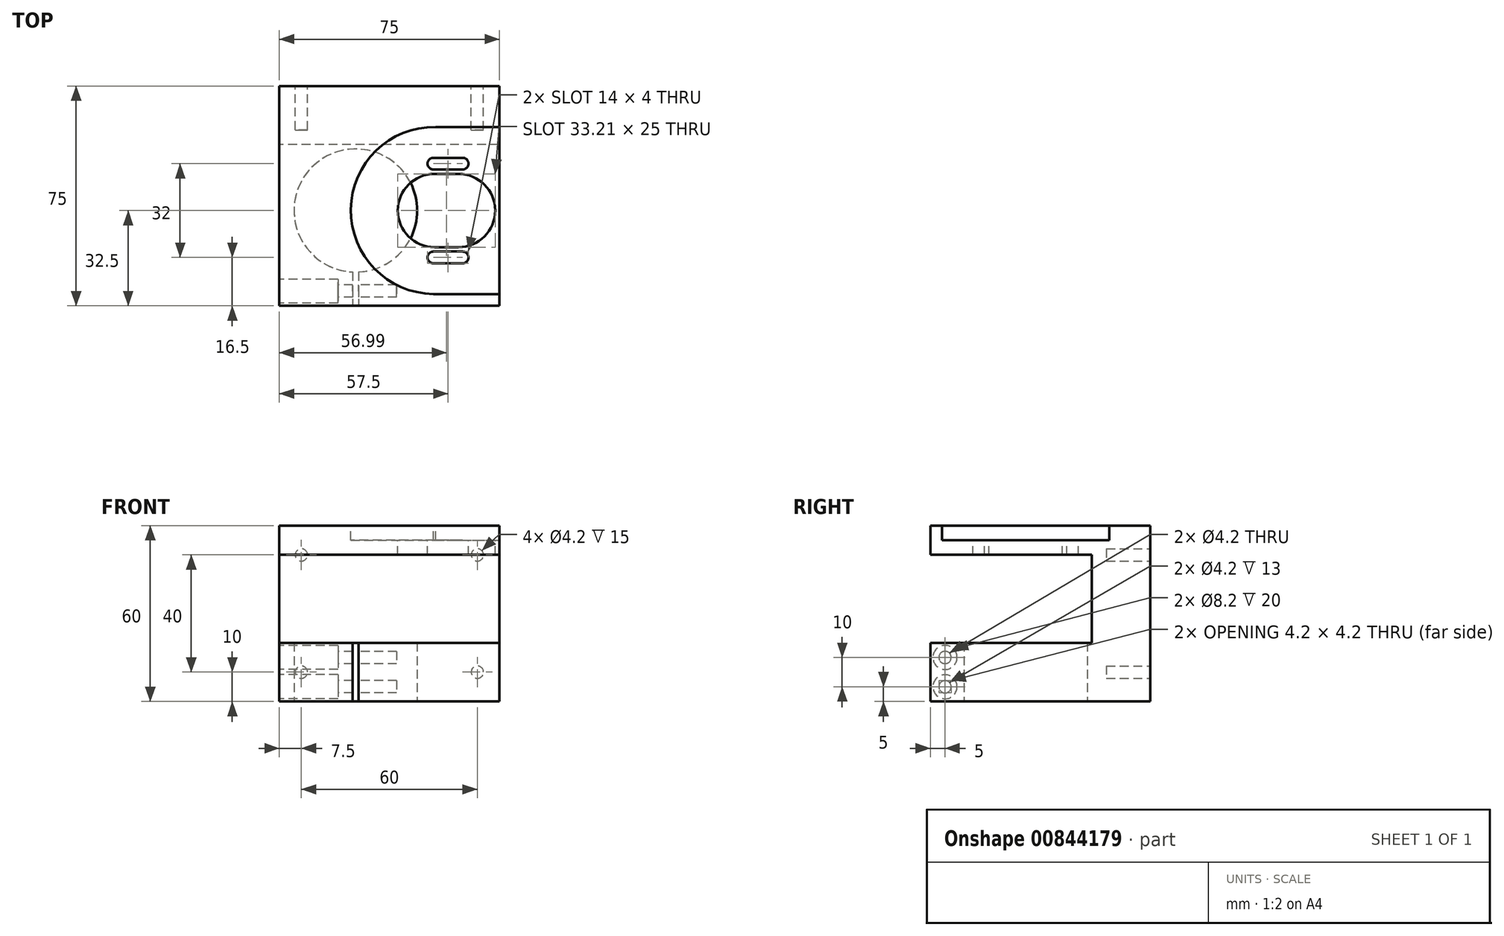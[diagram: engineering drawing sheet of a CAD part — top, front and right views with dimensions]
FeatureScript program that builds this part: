
annotation { "Feature Type Name" : "Feature", "Feature Type Description" : "" }
export const myFeature = defineFeature(function(context is Context, id is Id, definition is map)
    precondition{}
    {
        {
            var Q0;
            Q0=qCreatedBy(makeId("Top.planeOp"),FACE);
            var sketch = newSketch(context, id + "F0", { "sketchPlane" : qUnion([Q0])});
            skLineSegment(sketch, "E0.bottom", {"start": v(37.5, -37.5) * mm, "end": v(-37.5, -37.5) * mm});
            skLineSegment(sketch, "E0.top", {"start": v(37.5, 37.5) * mm, "end": v(-37.5, 37.5) * mm});
            skLineSegment(sketch, "E0.left", {"start": v(37.5, -37.5) * mm, "end": v(37.5, 37.5) * mm});
            skLineSegment(sketch, "E0.right", {"start": v(-37.5, -37.5) * mm, "end": v(-37.5, 37.5) * mm});
            skPoint(sketch, "E0.middle", {"position": v(0, 0) * mm});
            skLineSegment(sketch, "E1", {"start": v(-37.5, 0) * mm, "end": v(37.5, 0) * mm, "construction": true});
            skSolve(sketch);
        }
        {
            var Q0;
            Q0=makeQuery(id+"F0.imprint","IMPRINT",FACE,{"disambiguationData":[TD([[makeQuery(id+"F0.imprint","IMPRINT",EDGE,{"derivedFrom":sQuery(id+"F0.wireOp",EDGE,"E0.bottom")}),-1.0]])]});
            extrude(context, id + "F1", {"entities" : qUnion([Q0]), "depth" : 60 * mm, "offsetDistance" : 25 * mm});
        }
        {
            var Q0;
            Q0=makeQuery(id+"F1.opExtrude","SWEPT_FACE",FACE,{"disambiguationData":[OSD([sQuery(id+"F0.wireOp",EDGE,"E0.right")])]});
            var sketch = newSketch(context, id + "F2", { "sketchPlane" : qUnion([Q0])});
            skLineSegment(sketch, "E2.bottom", {"start": v(-17.5, 20) * mm, "end": v(40.42, 20) * mm});
            skLineSegment(sketch, "E2.top", {"start": v(-17.5, 50) * mm, "end": v(40.42, 50) * mm});
            skLineSegment(sketch, "E2.left", {"start": v(-17.5, 20) * mm, "end": v(-17.5, 50) * mm});
            skLineSegment(sketch, "E2.right", {"start": v(40.42, 20) * mm, "end": v(40.42, 50) * mm});
            skSolve(sketch);
        }
        {
            var Q0;
            {var subQ0=sQuery(id+"F2.wireOp",EDGE,"E2.left");Q0=makeQuery(id+"F2.imprint","IMPRINT",FACE,{"disambiguationData":[TD([[makeQuery(id+"F2.imprint","IMPRINT",EDGE,{"derivedFrom":subQ0}),-1.0]])]});}
            extrude(context, id + "F3", {"entities" : qUnion([Q0]), "operationType" : NewBodyOperationType.REMOVE, "endBound" : BoundingType.THROUGH_ALL, "oppositeDirection" : true, "depth" : 25 * mm, "offsetDistance" : 25 * mm});
        }
        {
            var Q0;
            Q0=makeQuery(id+"F1.opExtrude","CAP_FACE",FACE,{"disambiguationData":[OSD([sQuery(id+"F0.wireOp",EDGE,"E0.bottom"),sQuery(id+"F0.wireOp",EDGE,"E0.top"),sQuery(id+"F0.wireOp",EDGE,"E0.left"),sQuery(id+"F0.wireOp",EDGE,"E0.right")])],"isStart":true});
            var sketch = newSketch(context, id + "F4", { "sketchPlane" : qUnion([Q0])});
            skArc(sketch, "E3", {"start": v(-12.5, 25.98) * mm, "mid": v(-11.5, -16) * mm, "end": v(-10.5, 25.98) * mm});
            skLineSegment(sketch, "E4", {"start": v(-11.5, 5) * mm, "end": v(-11.5, 46.8) * mm, "construction": true});
            skLineSegment(sketch, "E5.top", {"start": v(-10.5, 41.66) * mm, "end": v(-12.5, 41.66) * mm});
            skLineSegment(sketch, "E5.left", {"start": v(-10.5, 25.98) * mm, "end": v(-10.5, 41.66) * mm});
            skLineSegment(sketch, "E5.right", {"start": v(-12.5, 25.98) * mm, "end": v(-12.5, 41.66) * mm});
            skPoint(sketch, "E5.middle", {"position": v(-11.5, 31.6) * mm});
            skPoint(sketch, "E6.orphan", {"position": v(-10.5, 21.54) * mm});
            skPoint(sketch, "E5.bottom.end.orphan", {"position": v(-12.5, 21.54) * mm});
            skSolve(sketch);
        }
        {
            var Q0;
            {var subQ0=sQuery(id+"F4.wireOp",EDGE,"E3");Q0=makeQuery(id+"F4.imprint","IMPRINT",FACE,{"disambiguationData":[TD([[makeQuery(id+"F4.imprint","IMPRINT",EDGE,{"derivedFrom":subQ0}),1.0]])]});}
            extrude(context, id + "F5", {"entities" : qUnion([Q0]), "operationType" : NewBodyOperationType.REMOVE, "oppositeDirection" : true, "depth" : 25 * mm, "offsetDistance" : 25 * mm});
        }
        {
            var Q0;
            Q0=makeQuery(id+"F1.opExtrude","SWEPT_FACE",FACE,{"disambiguationData":[OSD([sQuery(id+"F0.wireOp",EDGE,"E0.right")])]});
            var sketch = newSketch(context, id + "F6", { "sketchPlane" : qUnion([Q0])});
            skLineSegment(sketch, "E7", {"start": v(32.5, 20) * mm, "end": v(32.5, 0) * mm, "construction": true});
            skCircle(sketch, "E8", {"center": v(32.5, 15) * mm, "radius": 2.1 * mm});
            skCircle(sketch, "E9", {"center": v(32.5, 5) * mm, "radius": 2.1 * mm});
            skLineSegment(sketch, "E10", {"start": v(37.5, 10) * mm, "end": v(22, 10) * mm, "construction": true});
            skPoint(sketch, "E10.endSnap0", {"position": v(32.5, 10) * mm});
            skSolve(sketch);
        }
        {
            var Q0;
            Q0=qSketchRegion(id+"F6",true);
            extrude(context, id + "F7", {"entities" : qUnion([Q0]), "operationType" : NewBodyOperationType.REMOVE, "oppositeDirection" : true, "depth" : 40 * mm, "offsetDistance" : 25 * mm});
        }
        {
            var Q0;
            Q0=makeQuery(id+"F1.opExtrude","SWEPT_FACE",FACE,{"disambiguationData":[OSD([sQuery(id+"F0.wireOp",EDGE,"E0.right")])]});
            var sketch = newSketch(context, id + "F8", { "sketchPlane" : qUnion([Q0])});
            skCircle(sketch, "E11", {"center": v(32.5, 15) * mm, "radius": 4.1 * mm});
            skCircle(sketch, "E12", {"center": v(32.5, 5) * mm, "radius": 4.1 * mm});
            skSolve(sketch);
        }
        {
            var Q0;
            Q0=makeQuery(id+"F8.imprint","IMPRINT",FACE,{"disambiguationData":[TD([[makeQuery(id+"F8.imprint","IMPRINT",EDGE,{"derivedFrom":sQuery(id+"F8.wireOp",EDGE,"E11")}),1.0]])]});
            var Q1;
            Q1=makeQuery(id+"F8.imprint","IMPRINT",FACE,{"disambiguationData":[TD([[makeQuery(id+"F8.imprint","IMPRINT",EDGE,{"derivedFrom":sQuery(id+"F8.wireOp",EDGE,"E12")}),1.0]])]});
            extrude(context, id + "F9", {"entities" : qUnion([Q0, Q1]), "operationType" : NewBodyOperationType.REMOVE, "oppositeDirection" : true, "depth" : 20 * mm, "offsetDistance" : 25 * mm});
        }
        {
            var Q0;
            Q0=makeQuery(id+"F1.opExtrude","CAP_FACE",FACE,{"disambiguationData":[OSD([sQuery(id+"F0.wireOp",EDGE,"E0.bottom"),sQuery(id+"F0.wireOp",EDGE,"E0.top"),sQuery(id+"F0.wireOp",EDGE,"E0.left"),sQuery(id+"F0.wireOp",EDGE,"E0.right")])],"isStart":false});
            var sketch = newSketch(context, id + "F10", { "sketchPlane" : qUnion([Q0])});
            skLineSegment(sketch, "E13", {"start": v(-1.64, -5) * mm, "end": v(42.67, -5) * mm, "construction": true});
            skLineSegment(sketch, "E14", {"start": v(20, 7.06) * mm, "end": v(20, -13.87) * mm, "construction": true});
            skLineSegment(sketch, "E15", {"start": v(15, 11) * mm, "end": v(25, 11) * mm});
            skLineSegment(sketch, "E16", {"start": v(15, -21) * mm, "end": v(25, -21) * mm});
            skArc(sketch, "E17.0.startCap", {"start": v(15, 9) * mm, "mid": v(13, 11) * mm, "end": v(15, 13) * mm});
            skArc(sketch, "E17.0.endCap", {"start": v(25, 13) * mm, "mid": v(27, 11) * mm, "end": v(25, 9) * mm});
            skLineSegment(sketch, "E17.0.left", {"start": v(15, 13) * mm, "end": v(25, 13) * mm});
            skLineSegment(sketch, "E17.0.right", {"start": v(15, 9) * mm, "end": v(25, 9) * mm});
            skArc(sketch, "E18.0.startCap", {"start": v(15, -23) * mm, "mid": v(13, -21) * mm, "end": v(15, -19) * mm});
            skArc(sketch, "E18.0.endCap", {"start": v(25, -19) * mm, "mid": v(27, -21) * mm, "end": v(25, -23) * mm});
            skLineSegment(sketch, "E18.0.left", {"start": v(15, -19) * mm, "end": v(25, -19) * mm});
            skLineSegment(sketch, "E18.0.right", {"start": v(15, -23) * mm, "end": v(25, -23) * mm});
            skArc(sketch, "E19", {"start": v(23.6, -17.5) * mm, "mid": v(36.1, -5) * mm, "end": v(23.6, 7.5) * mm});
            skLineSegment(sketch, "E20", {"start": v(15.38, 7.5) * mm, "end": v(23.6, 7.5) * mm});
            skLineSegment(sketch, "E21", {"start": v(15.38, -17.5) * mm, "end": v(23.6, -17.5) * mm});
            skArc(sketch, "E22.trimOffspring", {"start": v(15.38, 7.5) * mm, "mid": v(2.88, -5) * mm, "end": v(15.38, -17.5) * mm});
            skSolve(sketch);
        }
        {
            var Q0;
            Q0=qSketchRegion(id+"F10",true);
            extrude(context, id + "F11", {"entities" : qUnion([Q0]), "operationType" : NewBodyOperationType.REMOVE, "oppositeDirection" : true, "depth" : 25 * mm, "offsetDistance" : 25 * mm});
        }
        {
            var Q0;
            Q0=makeQuery(id+"F1.opExtrude","CAP_FACE",FACE,{"disambiguationData":[OSD([sQuery(id+"F0.wireOp",EDGE,"E0.bottom"),sQuery(id+"F0.wireOp",EDGE,"E0.top"),sQuery(id+"F0.wireOp",EDGE,"E0.left"),sQuery(id+"F0.wireOp",EDGE,"E0.right")])],"isStart":false});
            var sketch = newSketch(context, id + "F12", { "sketchPlane" : qUnion([Q0])});
            skArc(sketch, "E23", {"start": v(15.77, 23.5) * mm, "mid": v(-13.11, -4.62) * mm, "end": v(15, -33.5) * mm});
            skLineSegment(sketch, "E24.bottom", {"start": v(15, 23.5) * mm, "end": v(72, 23.5) * mm});
            skLineSegment(sketch, "E24.top", {"start": v(15, -33.5) * mm, "end": v(72, -33.5) * mm});
            skLineSegment(sketch, "E24.left", {"start": v(15, -33.5) * mm, "end": v(15, -33.5) * mm});
            skLineSegment(sketch, "E24.right", {"start": v(72, 23.5) * mm, "end": v(72, -33.5) * mm});
            skSolve(sketch);
        }
        {
            var Q0;
            Q0=qSketchRegion(id+"F12",true);
            extrude(context, id + "F13", {"entities" : qUnion([Q0]), "operationType" : NewBodyOperationType.REMOVE, "oppositeDirection" : true, "depth" : 5 * mm, "offsetDistance" : 25 * mm});
        }
        {
            var Q0;
            Q0=makeQuery(id+"F1.opExtrude","SWEPT_FACE",FACE,{"disambiguationData":[OSD([sQuery(id+"F0.wireOp",EDGE,"E0.top")])]});
            var sketch = newSketch(context, id + "F14", { "sketchPlane" : qUnion([Q0])});
            skLineSegment(sketch, "E25", {"start": v(0, 60) * mm, "end": v(0, 0) * mm, "construction": true});
            skLineSegment(sketch, "E26.bottom", {"start": v(30, 10) * mm, "end": v(-30, 10) * mm, "construction": true});
            skLineSegment(sketch, "E26.top", {"start": v(30, 50) * mm, "end": v(-30, 50) * mm, "construction": true});
            skLineSegment(sketch, "E26.left", {"start": v(30, 10) * mm, "end": v(30, 50) * mm, "construction": true});
            skLineSegment(sketch, "E26.right", {"start": v(-30, 10) * mm, "end": v(-30, 50) * mm, "construction": true});
            skPoint(sketch, "E26.middle", {"position": v(0, 30) * mm});
            skCircle(sketch, "E27", {"center": v(-30, 50) * mm, "radius": 2.1 * mm});
            skCircle(sketch, "E28", {"center": v(30, 50) * mm, "radius": 2.1 * mm});
            skCircle(sketch, "E29", {"center": v(30, 10) * mm, "radius": 2.1 * mm});
            skCircle(sketch, "E30", {"center": v(-30, 10) * mm, "radius": 2.1 * mm});
            skSolve(sketch);
        }
        {
            var Q0;
            Q0=qSketchRegion(id+"F14",true);
            extrude(context, id + "F15", {"entities" : qUnion([Q0]), "operationType" : NewBodyOperationType.REMOVE, "oppositeDirection" : true, "depth" : 15 * mm, "offsetDistance" : 25 * mm});
        }
    });
